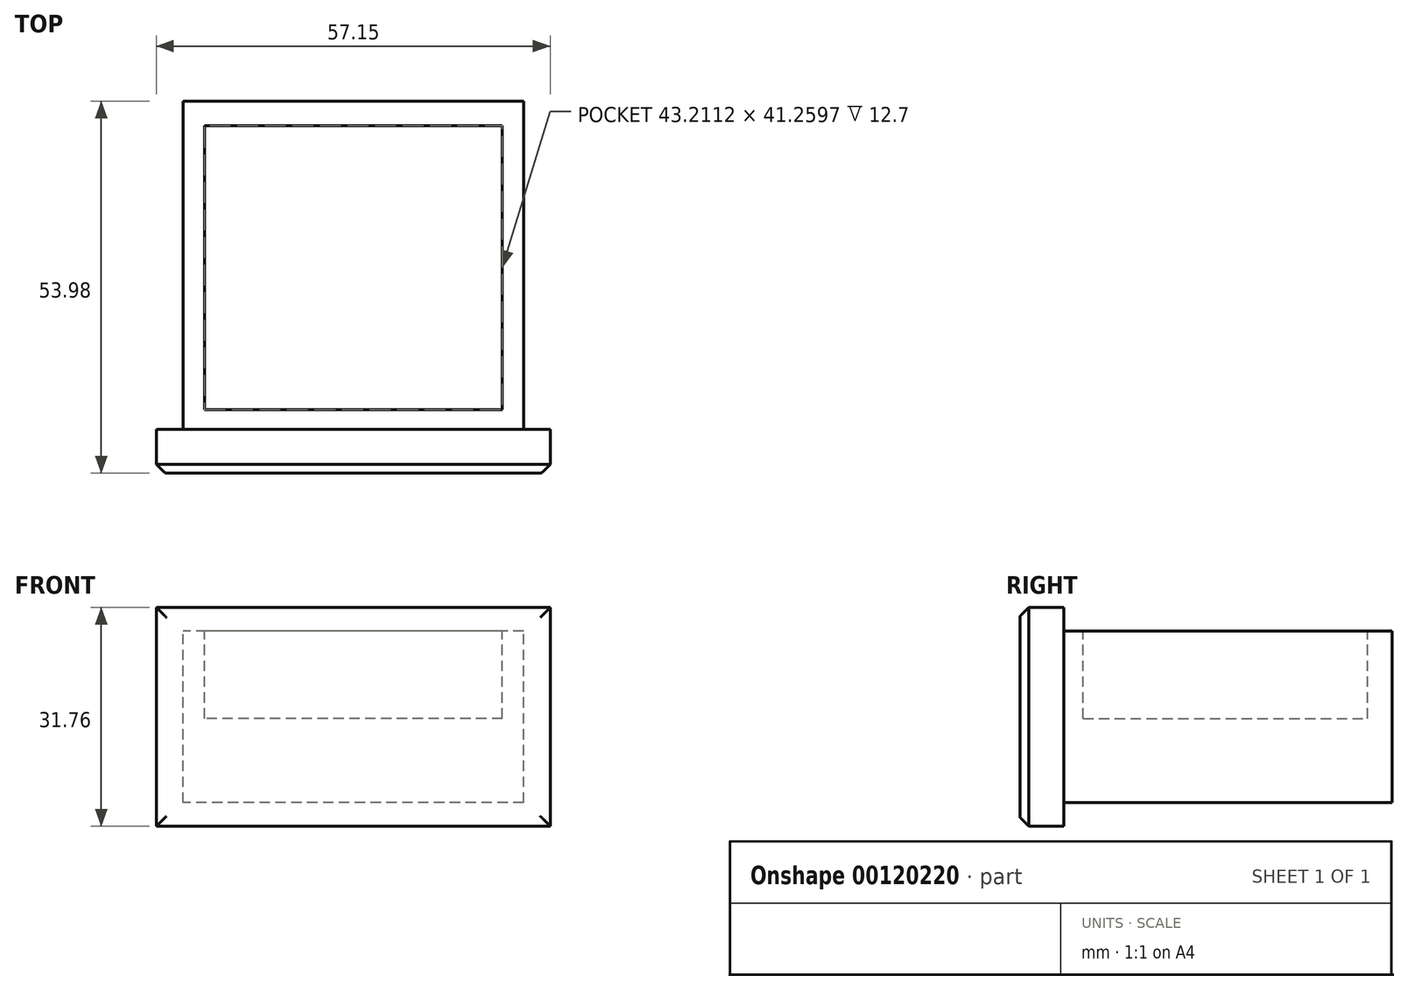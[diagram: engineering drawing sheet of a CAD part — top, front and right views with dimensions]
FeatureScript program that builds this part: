
annotation { "Feature Type Name" : "Feature", "Feature Type Description" : "" }
export const myFeature = defineFeature(function(context is Context, id is Id, definition is map)
    precondition{}
    {
        {
            var Q0;
            Q0=qCreatedBy(makeId("Front.planeOp"),FACE);
            var sketch = newSketch(context, id + "F0", { "sketchPlane" : qUnion([Q0])});
            skLineSegment(sketch, "E0.bottom", {"start": v(28.58, -15.87) * mm, "end": v(-28.57, -15.88) * mm});
            skLineSegment(sketch, "E0.top", {"start": v(28.57, 15.88) * mm, "end": v(-28.58, 15.88) * mm});
            skLineSegment(sketch, "E0.left", {"start": v(28.58, -15.88) * mm, "end": v(28.57, 15.88) * mm});
            skLineSegment(sketch, "E0.right", {"start": v(-28.57, -15.88) * mm, "end": v(-28.58, 15.88) * mm});
            skPoint(sketch, "E0.middle", {"position": v(0, 0) * mm});
            skSolve(sketch);
        }
        {
            var Q0;
            Q0=makeQuery(id+"F0.imprint","IMPRINT",FACE,{"disambiguationData":[TD([[makeQuery(id+"F0.imprint","IMPRINT",EDGE,{"derivedFrom":sQuery(id+"F0.wireOp",EDGE,"E0.bottom")}),-1.0]])]});
            extrude(context, id + "F1", {"entities" : qUnion([Q0]), "endBound" : BoundingType.SYMMETRIC, "depth" : 6.35 * mm});
        }
        {
            var Q0;
            Q0=qCreatedBy(makeId("Front.planeOp"),FACE);
            var sketch = newSketch(context, id + "F2", { "sketchPlane" : qUnion([Q0])});
            skLineSegment(sketch, "E1.bottom", {"start": v(24.7, -12.47) * mm, "end": v(-24.7, -12.47) * mm});
            skLineSegment(sketch, "E1.top", {"start": v(24.7, 12.47) * mm, "end": v(-24.7, 12.47) * mm});
            skLineSegment(sketch, "E1.left", {"start": v(24.7, -12.47) * mm, "end": v(24.7, 12.47) * mm});
            skLineSegment(sketch, "E1.right", {"start": v(-24.7, -12.47) * mm, "end": v(-24.7, 12.47) * mm});
            skPoint(sketch, "E1.middle", {"position": v(0, 0) * mm});
            skSolve(sketch);
        }
        {
            var Q0;
            Q0 = qSketchRegion(id + "F2", true);
            extrude(context, id + "F3", {"entities" : qUnion([Q0]), "operationType" : NewBodyOperationType.ADD, "oppositeDirection" : true, "depth" : 50.8 * mm});
        }
        {
            var Q0;
            Q0=makeQuery(id+"F3.opExtrude","SWEPT_FACE",FACE,{"disambiguationData":[OSD([sQuery(id+"F2.wireOp",EDGE,"E1.top")])]});
            var sketch = newSketch(context, id + "F4", { "sketchPlane" : qUnion([Q0])});
            skLineSegment(sketch, "E2.bottom", {"start": v(21.6, 6) * mm, "end": v(-21.6, 6) * mm});
            skLineSegment(sketch, "E2.top", {"start": v(21.6, 47.25) * mm, "end": v(-21.6, 47.25) * mm});
            skLineSegment(sketch, "E2.left", {"start": v(21.6, 6) * mm, "end": v(21.6, 47.25) * mm});
            skLineSegment(sketch, "E2.right", {"start": v(-21.6, 6) * mm, "end": v(-21.6, 47.25) * mm});
            skPoint(sketch, "E2.middle", {"position": v(0, 26.62) * mm});
            skSolve(sketch);
        }
        {
            var Q0;
            Q0 = qSketchRegion(id + "F4", true);
            extrude(context, id + "F5", {"entities" : qUnion([Q0]), "operationType" : NewBodyOperationType.REMOVE, "oppositeDirection" : true, "depth" : 12.7 * mm});
        }
        {
            var Q0;
            Q0=makeQuery(id+"F1.opExtrude","CAP_EDGE",EDGE,{"disambiguationData":[OSD([sQuery(id+"F0.wireOp",EDGE,"E0.bottom")])],"isStart":false});
            var Q1;
            Q1=makeQuery(id+"F1.opExtrude","CAP_EDGE",EDGE,{"disambiguationData":[OSD([sQuery(id+"F0.wireOp",EDGE,"E0.right")])],"isStart":false});
            var Q2;
            Q2=makeQuery(id+"F1.opExtrude","CAP_EDGE",EDGE,{"disambiguationData":[OSD([sQuery(id+"F0.wireOp",EDGE,"E0.left")])],"isStart":false});
            var Q3;
            Q3=makeQuery(id+"F1.opExtrude","CAP_EDGE",EDGE,{"disambiguationData":[OSD([sQuery(id+"F0.wireOp",EDGE,"E0.top")])],"isStart":false});
            chamfer(context, id + "F6", {"entities" : qUnion([Q0, Q1, Q2, Q3]), "width" : 1.27 * mm, "tangentPropagation" : true});
        }
        {
            var Q0;
            Q0=makeQuery(id+"F1.opExtrude","CAP_FACE",FACE,{"disambiguationData":[OSD([sQuery(id+"F0.wireOp",EDGE,"E0.bottom"),sQuery(id+"F0.wireOp",EDGE,"E0.top"),sQuery(id+"F0.wireOp",EDGE,"E0.left"),sQuery(id+"F0.wireOp",EDGE,"E0.right")])],"isStart":false});
            fillet(context, id + "F7", {"entities" : qUnion([Q0]), "radius" : 0.5 * mm, "tangentPropagation" : true, "allowEdgeOverflow" : false});
        }
    });
